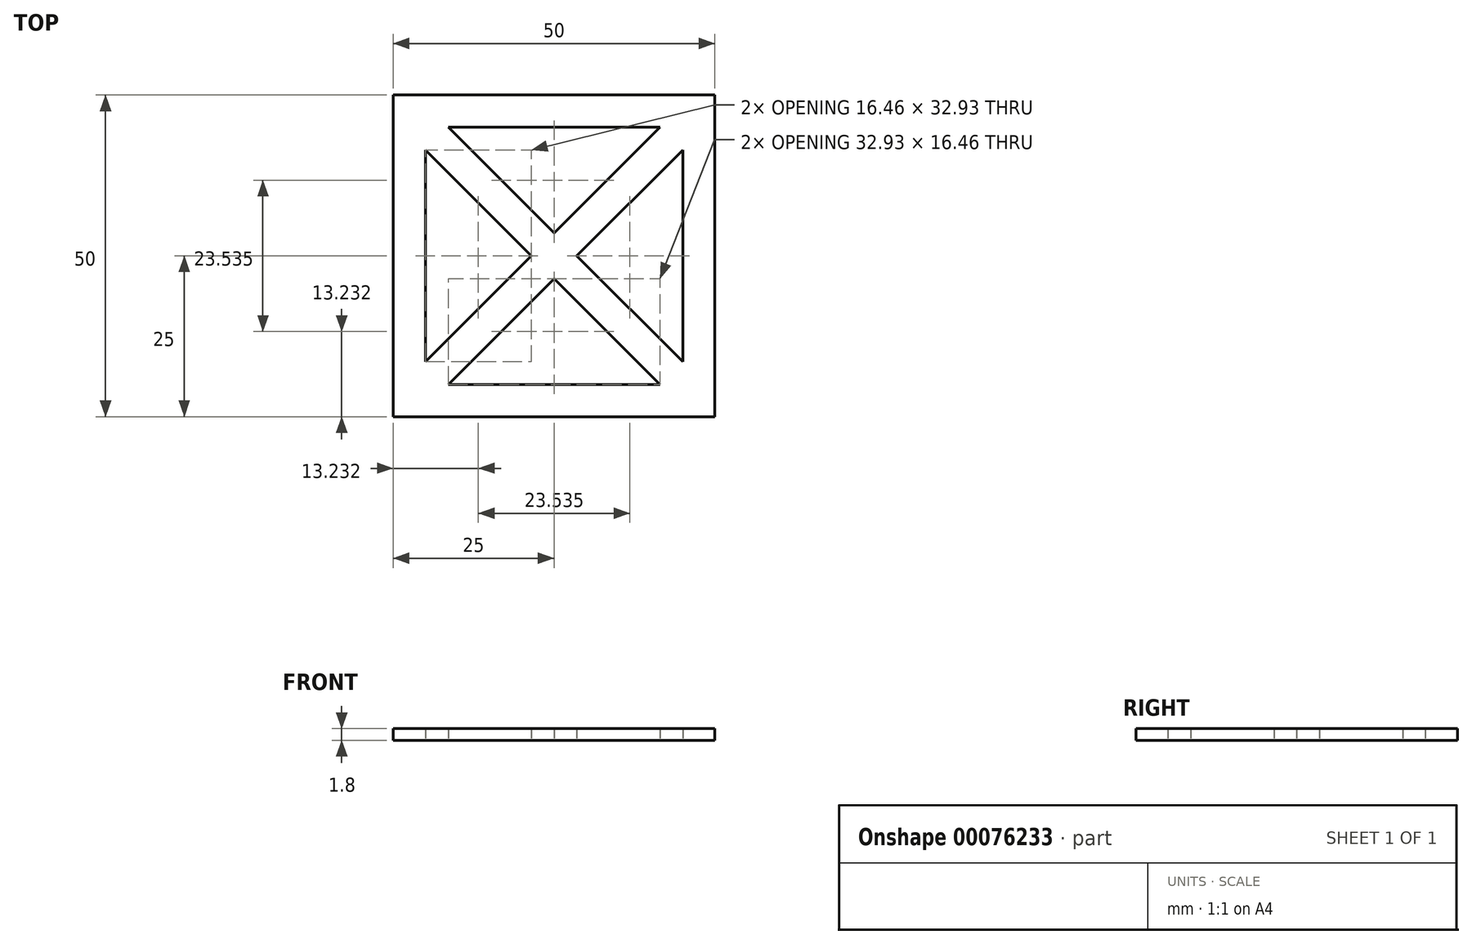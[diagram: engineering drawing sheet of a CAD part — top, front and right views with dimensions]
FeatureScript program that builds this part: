
annotation { "Feature Type Name" : "Feature", "Feature Type Description" : "" }
export const myFeature = defineFeature(function(context is Context, id is Id, definition is map)
    precondition{}
    {
        {
            var Q0;
            Q0=qCreatedBy(makeId("Top.planeOp"),FACE);
            var sketch = newSketch(context, id + "F0", { "sketchPlane" : qUnion([Q0])});
            skLineSegment(sketch, "E0.bottom", {"start": v(25, -25) * mm, "end": v(-25, -25) * mm});
            skLineSegment(sketch, "E0.top", {"start": v(25, 25) * mm, "end": v(-25, 25) * mm});
            skLineSegment(sketch, "E0.left", {"start": v(25, -25) * mm, "end": v(25, 25) * mm});
            skLineSegment(sketch, "E0.right", {"start": v(-25, -25) * mm, "end": v(-25, 25) * mm});
            skPoint(sketch, "E0.middle", {"position": v(0, 0) * mm});
            skLineSegment(sketch, "E1.bottom", {"start": v(20, -20) * mm, "end": v(-20, -20) * mm});
            skLineSegment(sketch, "E1.top", {"start": v(20, 20) * mm, "end": v(-20, 20) * mm});
            skLineSegment(sketch, "E1.left", {"start": v(20, -20) * mm, "end": v(20, 20) * mm});
            skLineSegment(sketch, "E1.right", {"start": v(-20, -20) * mm, "end": v(-20, 20) * mm});
            skLineSegment(sketch, "E2", {"start": v(-20, 20) * mm, "end": v(20, -20) * mm, "construction": true});
            skLineSegment(sketch, "E3", {"start": v(20, 20) * mm, "end": v(-20, -20) * mm, "construction": true});
            skLineSegment(sketch, "E4", {"start": v(-20, -16.46) * mm, "end": v(16.46, 20) * mm});
            skLineSegment(sketch, "E5", {"start": v(-16.46, 20) * mm, "end": v(20, -16.46) * mm});
            skLineSegment(sketch, "E6.MirrorCS", {"start": v(-20, 16.46) * mm, "end": v(16.46, -20) * mm});
            skLineSegment(sketch, "E7.MirrorCS", {"start": v(-16.46, -20) * mm, "end": v(20, 16.46) * mm});
            skSolve(sketch);
        }
        {
            var Q0;
            Q0 = qSketchRegion(id + "F0", true);
            var Q1;
            {var subQ1=sQuery(id+"F0.wireOp",EDGE,"E1.top");var subQ7=sQuery(id+"F0.wireOp",EDGE,"E1.right");var subQ8=makeQuery(id+"F0.imprint","INTERSECT",VERTEX,{"derivedFrom":[subQ1,subQ7]});Q1=makeQuery(id+"F0.imprint","IMPRINT",FACE,{"disambiguationData":[TD([[makeQuery(id+"F0.imprint","IMPRINT",EDGE,{"disambiguationData":[TD([[subQ8,1.0]])],"derivedFrom":subQ1}),1.0]])]});}
            var Q2;
            {var subQ1=sQuery(id+"F0.wireOp",EDGE,"E1.bottom");var subQ5=sQuery(id+"F0.wireOp",EDGE,"E1.left");var subQ6=makeQuery(id+"F0.imprint","INTERSECT",VERTEX,{"derivedFrom":[subQ1,subQ5]});Q2=makeQuery(id+"F0.imprint","IMPRINT",FACE,{"disambiguationData":[TD([[makeQuery(id+"F0.imprint","IMPRINT",EDGE,{"disambiguationData":[TD([[subQ6,-1.0]])],"derivedFrom":subQ1}),-1.0]])]});}
            var Q3;
            {var subQ0=sQuery(id+"F0.wireOp",EDGE,"E6.MirrorCS");var subQ1=sQuery(id+"F0.wireOp",EDGE,"E4");var subQ2=makeQuery(id+"F0.imprint","INTERSECT",VERTEX,{"derivedFrom":[subQ1,subQ0]});Q3=makeQuery(id+"F0.imprint","IMPRINT",FACE,{"disambiguationData":[TD([[makeQuery(id+"F0.imprint","IMPRINT",EDGE,{"disambiguationData":[TD([[subQ2,-1.0]])],"derivedFrom":subQ1}),-1.0]])]});}
            var Q4;
            {var subQ1=sQuery(id+"F0.wireOp",EDGE,"E1.top");var subQ5=sQuery(id+"F0.wireOp",EDGE,"E1.left");var subQ6=makeQuery(id+"F0.imprint","INTERSECT",VERTEX,{"derivedFrom":[subQ1,subQ5]});Q4=makeQuery(id+"F0.imprint","IMPRINT",FACE,{"disambiguationData":[TD([[makeQuery(id+"F0.imprint","IMPRINT",EDGE,{"disambiguationData":[TD([[subQ6,-1.0]])],"derivedFrom":subQ1}),1.0]])]});}
            var Q5;
            {var subQ5=sQuery(id+"F0.wireOp",EDGE,"E1.right");var subQ7=sQuery(id+"F0.wireOp",EDGE,"E1.bottom");var subQ8=makeQuery(id+"F0.imprint","INTERSECT",VERTEX,{"derivedFrom":[subQ7,subQ5]});Q5=makeQuery(id+"F0.imprint","IMPRINT",FACE,{"disambiguationData":[TD([[makeQuery(id+"F0.imprint","IMPRINT",EDGE,{"disambiguationData":[TD([[subQ8,1.0]])],"derivedFrom":subQ7}),-1.0]])]});}
            extrude(context, id + "F1", {"entities" : qUnion([Q0, Q1, Q2, Q3, Q4, Q5]), "depth" : 1.8 * mm});
        }
    });
